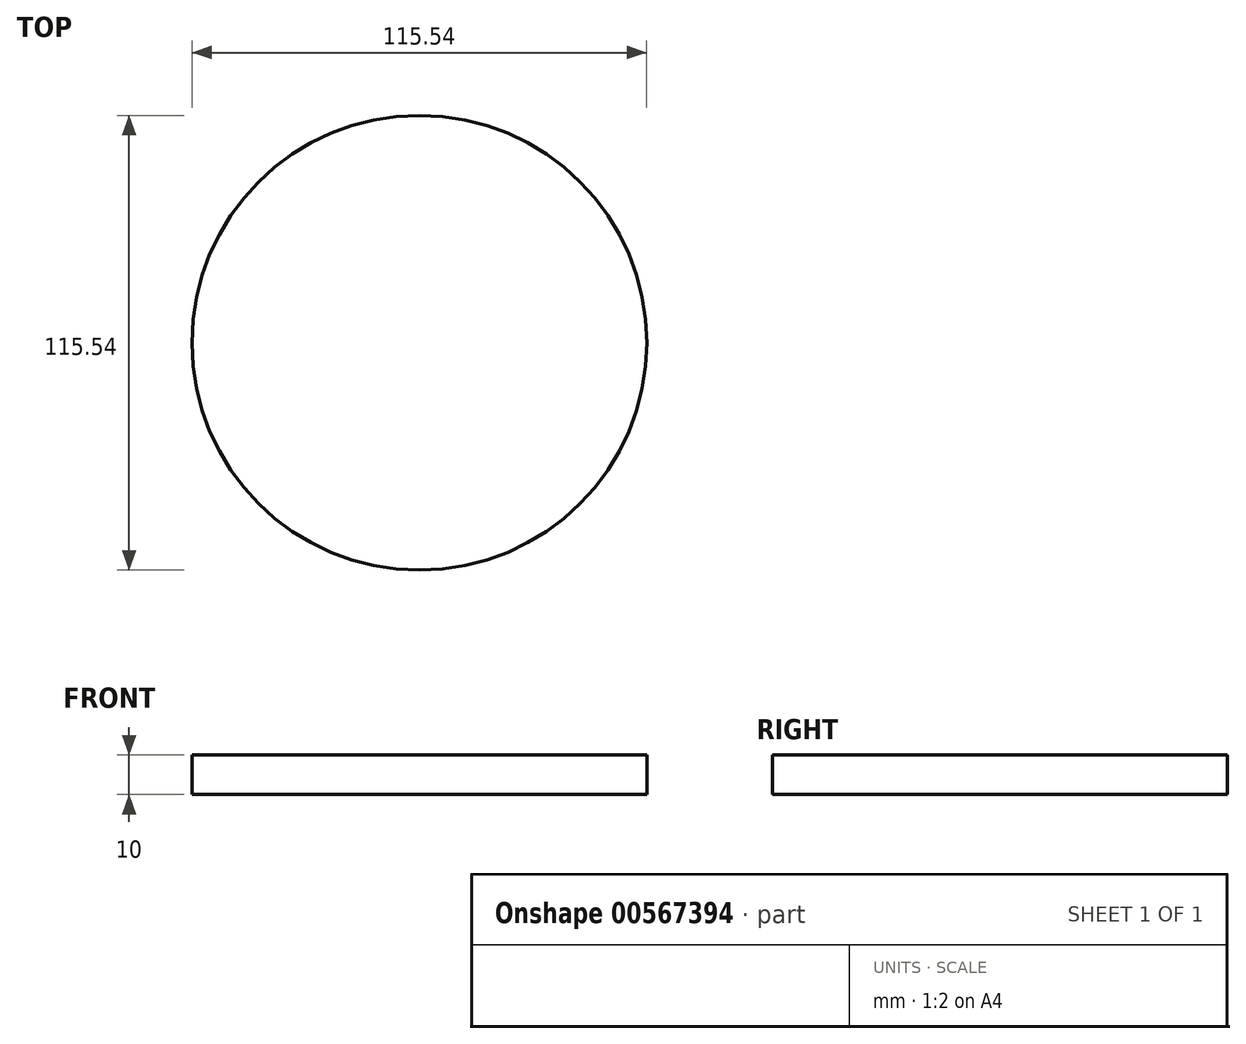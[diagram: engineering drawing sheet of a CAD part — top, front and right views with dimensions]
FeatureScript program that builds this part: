
annotation { "Feature Type Name" : "Feature", "Feature Type Description" : "" }
export const myFeature = defineFeature(function(context is Context, id is Id, definition is map)
    precondition{}
    {
        {
            var Q0;
            Q0=qCreatedBy(makeId("Top.planeOp"),FACE);
            var sketch = newSketch(context, id + "F0", { "sketchPlane" : qUnion([Q0])});
            skCircle(sketch, "E0", {"center": v(0, 0) * mm, "radius": 57.77 * mm});
            skCircle(sketch, "E1.cCircle", {"center": v(0, 0) * mm, "radius": 57.77 * mm, "construction": true});
            skPoint(sketch, "E2.end.orphan", {"position": v(0, -57.77) * mm});
            skSolve(sketch);
        }
        {
            var Q0;
            Q0 = qSketchRegion(id + "F0", true);
            extrude(context, id + "F1", {"entities" : qUnion([Q0]), "depth" : 10 * mm, "offsetDistance" : 25 * mm});
        }
        {
            var Q0;
            Q0=makeQuery(id+"F1.opExtrude","CAP_FACE",FACE,{"disambiguationData":[OSD([sQuery(id+"F0.wireOp",EDGE,"E0")])],"isStart":false});
            var sketch = newSketch(context, id + "F2", { "sketchPlane" : qUnion([Q0])});
            skCircle(sketch, "E3.cCircle", {"center": v(0, 0) * mm, "radius": 57.77 * mm, "construction": true});
            skLineSegment(sketch, "E4", {"start": v(0, 0) * mm, "end": v(0, 57.77) * mm});
            skLineSegment(sketch, "E5", {"start": v(0, 0) * mm, "end": v(45.17, 36.02) * mm});
            skLineSegment(sketch, "E6", {"start": v(0, 0) * mm, "end": v(56.32, -12.86) * mm});
            skLineSegment(sketch, "E7", {"start": v(0, 0) * mm, "end": v(25.07, -52.05) * mm});
            skLineSegment(sketch, "E8", {"start": v(0, 0) * mm, "end": v(-25.07, -52.05) * mm});
            skLineSegment(sketch, "E9", {"start": v(0, 0) * mm, "end": v(-56.32, -12.86) * mm});
            skLineSegment(sketch, "E10", {"start": v(0, 0) * mm, "end": v(-45.17, 36.02) * mm});
            skSolve(sketch);
        }
    });
